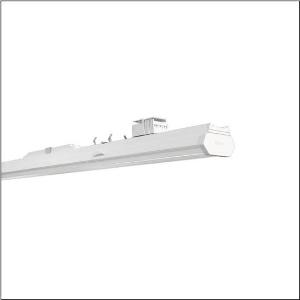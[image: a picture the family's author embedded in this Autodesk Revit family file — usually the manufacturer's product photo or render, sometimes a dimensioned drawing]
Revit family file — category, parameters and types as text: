
# Revit family: licross_11_protected_mo_51tp12dn595g
name_source: partatom
category: Lighting Fixtures
units: mm (PartAtom-declared; Revit-internal decimal feet)

## family parameters
Cut with Voids When Loaded = No
Host = Face
Light Source = No
Part Type = Normal
Room Calculation Point = No
Round Connector Dimension = Use Diameter
Shared = No

## types (1)
- --- (1 x LED, 9820 lm, 57.1 W, 5000K)
    Apparent Load = 57 VA
    CIE Flux Codes = 73 92 98 99 100
    Color Rendering = 80
    Color Temperature = 5000K
    Default Elevation = 1800 mm
    Description = Licross 11 Protected MO, luminaire insert, of sheet steel, galvanised, coil coated, white, length: 1.500mm, width: 90mm, height: 101mm, LED rated luminous flux: 9.820lm, light colour: 850, SDCM (Standard Deviation of Colour Matching)MacAdam ≤ 2 SDCM (initial), control gear: DALI 2, with plug, 5-pole, with phase selection, mains connection: 220..240V, AC, 50/60Hz, rated input power: 57W, internal wiring halogen-free, primary optical cover: cover, of PMMA, light emission: direct distribution, primary light characteristic: symmetric, protection rating (complete): IP64, insulation class (complete): insulation class I (protective earthing), certification: CE, ENEC, VDE, UKCA, protection symbol: D if used in an environment with conductive dust loads with corresponding accessories, impact resistance: IK06, permissible ambient temperature for indoor applications: -25..+35°C, corresponds to IFS (International Featured Standards) requirements for safety and quality in the food industry, reducing of maximum allowable ambient temperature of 5°C with ceiling mounting, LABS conformity tested according to VDMA 24364:2018-05, The light source and the operating device comply with the requirements of the Ecodesign Regulation (EU) 2019/2020 and are replaceable in accordance with this regulation, packaging unit: 1 piece
    Height = 92 mm
    Lamp = 1 x LED
    Lamp Light Flux = 9820 lm
    Lamp Power = 57.1 W
    Lamp count = 1
    Length = 1500 mm
    Luminous efficacy = 172 lm/W
    Manufacturer = Siteco
    ModVariant = No
    Model = 51TP12DN595G
    Mounting Place = Ceiling
    Mounting Type = Pendant
    Number of Poles = 1
    OnlyDefault = Yes
    Power Factor = 1
    Product Name = Licross 11 Protected MO
    Product group = luminaire insert | ceiling pendant
    ProductGroupID = 901
    Protection Class = Protection class I
    Protection Degree = IP 64
    RLX_Detail_Level = 1
    RLX_Emergency_Light_Flux = 0 lm
    RLX_Emergency_Type = 0
    RLX_Emergency_Type_DB = No
    RlxData = <blob elided: 24625 chars, md5=3945d5ab>
    Socket = socket
    Standby Power = 0 W
    System Light Flux = 9820 lm
    System Power = 57 W
    Type Comments = factory setting: luminous flux: 100 % | dim-lin: 254 | 378 mA
    Type Image = l_1256148.jpg
    URL = http://relux.com
    VarID = @adj_039037
    Voltage = 0 V
    Weight = 0.00 kg
    Width = 88 mm

## geometry (parser evidence)
native form markers: Blend x4, Sweep x10
no freeform markers — native parametric forms only
